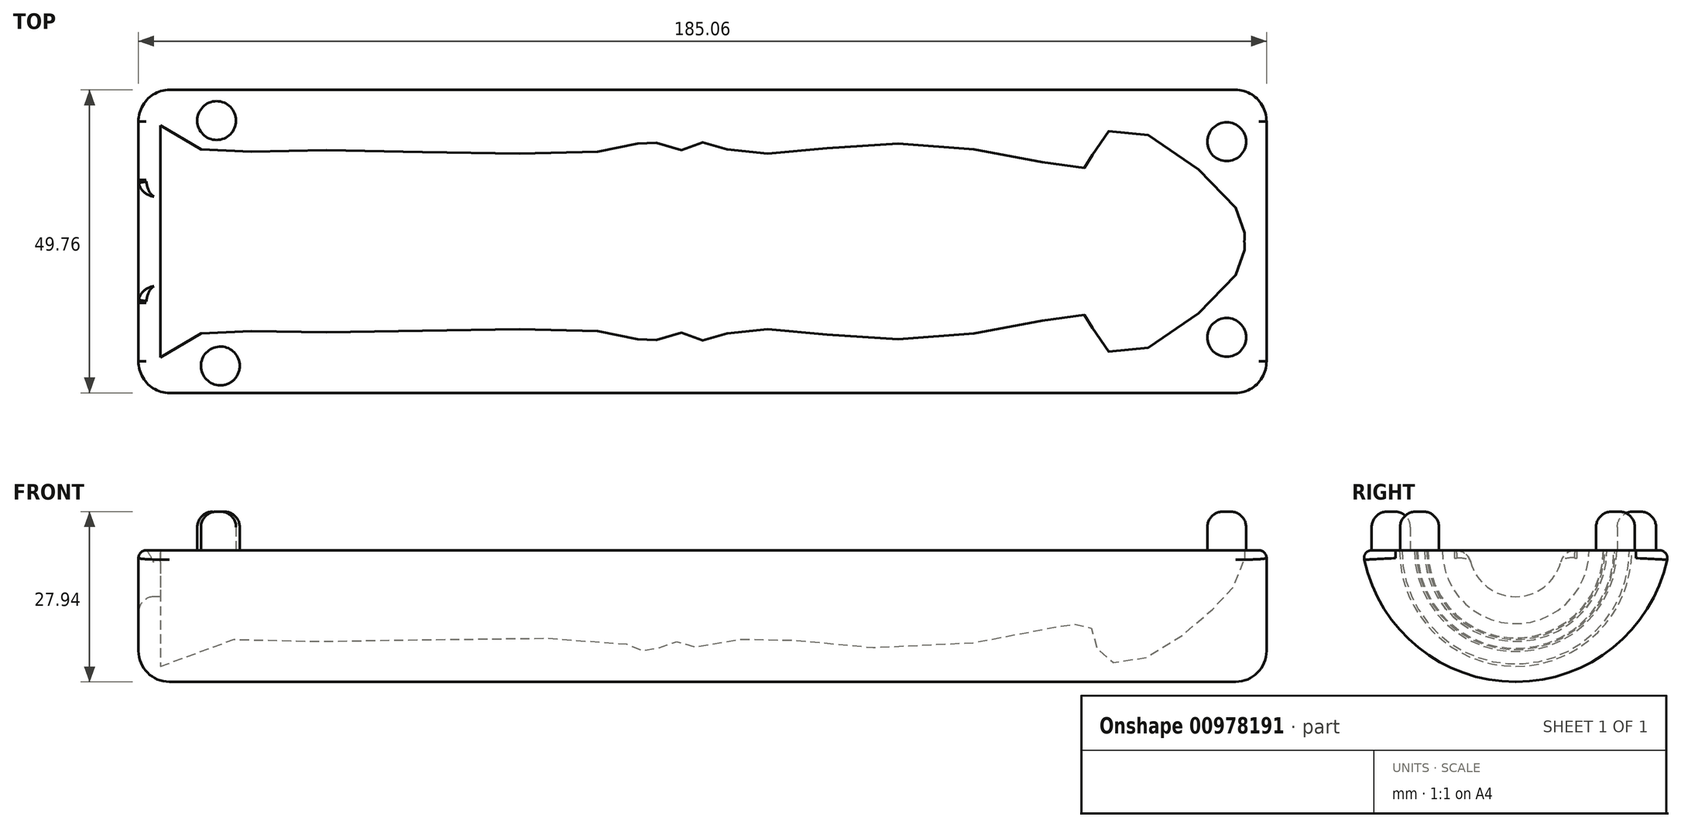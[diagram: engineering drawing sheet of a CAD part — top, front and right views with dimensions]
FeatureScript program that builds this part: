
annotation { "Feature Type Name" : "Feature", "Feature Type Description" : "" }
export const myFeature = defineFeature(function(context is Context, id is Id, definition is map)
    precondition{}
    {
        {
            var Q0;
            Q0=qCreatedBy(makeId("Front.planeOp"),FACE);
            var sketch = newSketch(context, id + "F0", { "sketchPlane" : qUnion([Q0])});
            skLineSegment(sketch, "E0.right", {"start": v(-88.9, 19.05) * mm, "end": v(-88.9, 0) * mm});
            skPoint(sketch, "E0.middle", {"position": v(0, 0) * mm});
            skLineSegment(sketch, "E1", {"start": v(-88.9, 0) * mm, "end": v(88.9, 0) * mm});
            skFitSpline(sketch, "E2", {"points": [v(-88.9, 19.05) * mm, v(-68.88, 14.9) * mm, v(-12.62, 15.36) * mm, v(-8.8, 16.59) * mm, v(-3.86, 14.96) * mm, v(0, 16.28) * mm, v(6.03, 14.62) * mm, v(37.07, 15.98) * mm, v(63.33, 12.23) * mm, v(64, 14.28) * mm, v(68.77, 18.66) * mm, v(87.5, 5.49) * mm, v(88.9, 0) * mm], "startDerivative": vector(153.99, -157.05) * mm, "endDerivative": vector(-4.41, -120.62) * mm});
            skSolve(sketch);
        }
        {
            var Q0;
            Q0=makeQuery(id+"F0.imprint","IMPRINT",FACE,{"disambiguationData":[TD([[makeQuery(id+"F0.imprint","IMPRINT",EDGE,{"derivedFrom":sQuery(id+"F0.wireOp",EDGE,"E0.right")}),1.0]])]});
            var Q1;
            Q1=sQuery(id+"F0.wireOp",EDGE,"E1");
            revolve(context, id + "F1", {"surfaceOperationType" : NewSurfaceOperationType.NEW, "entities" : qUnion([Q0]), "axis" : qUnion([Q1]), "revolveType" : RevolveType.FULL});
        }
        {
            var Q0;
            Q0=qCreatedBy(makeId("Top.planeOp"),FACE);
            var sketch = newSketch(context, id + "F2", { "sketchPlane" : qUnion([Q0])});
            skLineSegment(sketch, "E3.bottom", {"start": v(89.99, 25.13) * mm, "end": v(-89.99, 25.13) * mm});
            skLineSegment(sketch, "E3.top", {"start": v(89.99, -25.13) * mm, "end": v(-89.99, -25.13) * mm});
            skLineSegment(sketch, "E3.left", {"start": v(92.53, 22.59) * mm, "end": v(92.53, -22.59) * mm});
            skLineSegment(sketch, "E3.right", {"start": v(-92.53, 22.59) * mm, "end": v(-92.53, -22.59) * mm});
            skPoint(sketch, "E3.middle", {"position": v(0, 0) * mm});
            skPoint(sketch, "E4.visualSharp", {"position": v(-92.53, 25.13) * mm});
            skArc(sketch, "E4.filletArc", {"start": v(-89.99, 25.13) * mm, "mid": v(-91.78, 24.38) * mm, "end": v(-92.53, 22.59) * mm});
            skPoint(sketch, "E5.visualSharp", {"position": v(-92.53, -25.13) * mm});
            skArc(sketch, "E5.filletArc", {"start": v(-92.53, -22.59) * mm, "mid": v(-91.78, -24.38) * mm, "end": v(-89.99, -25.13) * mm});
            skPoint(sketch, "E6.visualSharp", {"position": v(92.53, 25.13) * mm});
            skArc(sketch, "E6.filletArc", {"start": v(92.53, 22.59) * mm, "mid": v(91.78, 24.38) * mm, "end": v(89.99, 25.13) * mm});
            skPoint(sketch, "E7.visualSharp", {"position": v(92.53, -25.13) * mm});
            skArc(sketch, "E7.filletArc", {"start": v(89.99, -25.13) * mm, "mid": v(91.78, -24.38) * mm, "end": v(92.53, -22.59) * mm});
            skCircle(sketch, "E8", {"center": v(86, 16.37) * mm, "radius": 3.18 * mm});
            skCircle(sketch, "E9", {"center": v(86, -15.77) * mm, "radius": 3.18 * mm});
            skCircle(sketch, "E10", {"center": v(-79.7, 19.84) * mm, "radius": 3.18 * mm});
            skCircle(sketch, "E11", {"center": v(-79.1, -20.45) * mm, "radius": 3.18 * mm});
            skSolve(sketch);
        }
        {
            var Q0;
            Q0=makeQuery(id+"F2.imprint","IMPRINT",FACE,{"disambiguationData":[TD([[makeQuery(id+"F2.imprint","IMPRINT",EDGE,{"derivedFrom":sQuery(id+"F2.wireOp",EDGE,"E3.bottom")}),1.0]])]});
            var Q1;
            Q1=makeQuery(id+"F2.imprint","IMPRINT",FACE,{"disambiguationData":[TD([[makeQuery(id+"F2.imprint","IMPRINT",EDGE,{"derivedFrom":sQuery(id+"F2.wireOp",EDGE,"E8")}),1.0]])]});
            var Q2;
            Q2=makeQuery(id+"F2.imprint","IMPRINT",FACE,{"disambiguationData":[TD([[makeQuery(id+"F2.imprint","IMPRINT",EDGE,{"derivedFrom":sQuery(id+"F2.wireOp",EDGE,"E9")}),1.0]])]});
            var Q3;
            Q3=makeQuery(id+"F2.imprint","IMPRINT",FACE,{"disambiguationData":[TD([[makeQuery(id+"F2.imprint","IMPRINT",EDGE,{"derivedFrom":sQuery(id+"F2.wireOp",EDGE,"E11")}),1.0]])]});
            var Q4;
            Q4=makeQuery(id+"F2.imprint","IMPRINT",FACE,{"disambiguationData":[TD([[makeQuery(id+"F2.imprint","IMPRINT",EDGE,{"derivedFrom":sQuery(id+"F2.wireOp",EDGE,"E10")}),1.0]])]});
            extrude(context, id + "F3", {"entities" : qUnion([Q0, Q1, Q2, Q3, Q4]), "oppositeDirection" : true, "depth" : 21.59 * mm, "offsetDistance" : 25.4 * mm});
        }
        {
            var Q0;
            Q0=makeQuery(id+"F1.opRevolve","SWEPT_BODY",BODY,{"disambiguationData":[OSD([sQuery(id+"F0.wireOp",EDGE,"E0.right"),sQuery(id+"F0.wireOp",EDGE,"E1"),sQuery(id+"F0.wireOp",EDGE,"E2")])]});
            var Q1;
            Q1=makeQuery(id+"F3.opExtrude","SWEPT_BODY",BODY,{"disambiguationData":[OSD([sQuery(id+"F2.wireOp",EDGE,"E3.bottom"),sQuery(id+"F2.wireOp",EDGE,"E3.top"),sQuery(id+"F2.wireOp",EDGE,"E3.left"),sQuery(id+"F2.wireOp",EDGE,"E3.right"),sQuery(id+"F2.wireOp",EDGE,"E4.filletArc"),sQuery(id+"F2.wireOp",EDGE,"E5.filletArc"),sQuery(id+"F2.wireOp",EDGE,"E6.filletArc"),sQuery(id+"F2.wireOp",EDGE,"E7.filletArc")])]});
            booleanBodies(context, id + "F4", {"operationType" : BooleanOperationType.SUBTRACTION, "tools" : qUnion([Q0]), "targets" : qUnion([Q1])});
        }
        {
            var Q0;
            Q0=makeQuery(id+"F3.opExtrude","CAP_EDGE",EDGE,{"disambiguationData":[OSD([sQuery(id+"F2.wireOp",EDGE,"E3.top")])],"isStart":false});
            var Q1;
            Q1=makeQuery(id+"F3.opExtrude","CAP_EDGE",EDGE,{"disambiguationData":[OSD([sQuery(id+"F2.wireOp",EDGE,"E3.bottom")])],"isStart":false});
            fillet(context, id + "F5", {"entities" : qUnion([Q0, Q1]), "radius" : 25.4 * mm, "allowEdgeOverflow" : false});
        }
        {
            var Q0;
            Q0=makeQuery(id+"F5.opFillet","BLEND_EDGE",EDGE,{"blendedFrom":[makeQuery(id+"F3.opExtrude","CAP_EDGE",EDGE,{"disambiguationData":[OSD([sQuery(id+"F2.wireOp",EDGE,"E3.bottom")])],"isStart":false}),makeQuery(id+"F3.opExtrude","SWEPT_FACE",FACE,{"disambiguationData":[OSD([sQuery(id+"F2.wireOp",EDGE,"E3.left")])]})],"blendedInto":[makeQuery(id+"F3.opExtrude","SWEPT_FACE",FACE,{"disambiguationData":[OSD([sQuery(id+"F2.wireOp",EDGE,"E3.left")])]})]});
            var Q1;
            Q1=makeQuery(id+"F5.opFillet","BLEND_EDGE",EDGE,{"blendedFrom":[makeQuery(id+"F3.opExtrude","CAP_EDGE",EDGE,{"disambiguationData":[OSD([sQuery(id+"F2.wireOp",EDGE,"E3.top")])],"isStart":false}),makeQuery(id+"F3.opExtrude","SWEPT_FACE",FACE,{"disambiguationData":[OSD([sQuery(id+"F2.wireOp",EDGE,"E3.right")])]})],"blendedInto":[makeQuery(id+"F3.opExtrude","SWEPT_FACE",FACE,{"disambiguationData":[OSD([sQuery(id+"F2.wireOp",EDGE,"E3.right")])]})]});
            fillet(context, id + "F6", {"entities" : qUnion([Q0, Q1]), "radius" : 5.08 * mm, "tangentPropagation" : true, "allowEdgeOverflow" : false});
        }
        {
            var Q0;
            {var subQ0=sQuery(id+"F2.wireOp",EDGE,"E3.top");Q0=makeQuery(id+"F5.opFillet","BLEND_EDGE",EDGE,{"blendedFrom":[makeQuery(id+"F3.opExtrude","CAP_EDGE",EDGE,{"disambiguationData":[OSD([subQ0])],"isStart":false}),makeQuery(id+"F3.opExtrude","CAP_FACE",FACE,{"disambiguationData":[OSD([sQuery(id+"F2.wireOp",EDGE,"E3.bottom"),subQ0,sQuery(id+"F2.wireOp",EDGE,"E3.left"),sQuery(id+"F2.wireOp",EDGE,"E3.right"),sQuery(id+"F2.wireOp",EDGE,"E4.filletArc"),sQuery(id+"F2.wireOp",EDGE,"E5.filletArc"),sQuery(id+"F2.wireOp",EDGE,"E6.filletArc"),sQuery(id+"F2.wireOp",EDGE,"E7.filletArc")])],"isStart":true})],"blendedInto":[makeQuery(id+"F3.opExtrude","CAP_FACE",FACE,{"disambiguationData":[OSD([sQuery(id+"F2.wireOp",EDGE,"E3.bottom"),subQ0,sQuery(id+"F2.wireOp",EDGE,"E3.left"),sQuery(id+"F2.wireOp",EDGE,"E3.right"),sQuery(id+"F2.wireOp",EDGE,"E4.filletArc"),sQuery(id+"F2.wireOp",EDGE,"E5.filletArc"),sQuery(id+"F2.wireOp",EDGE,"E6.filletArc"),sQuery(id+"F2.wireOp",EDGE,"E7.filletArc")])],"isStart":true})]});}
            fillet(context, id + "F7", {"entities" : qUnion([Q0]), "radius" : 1.27 * mm, "tangentPropagation" : true, "allowEdgeOverflow" : false});
        }
        {
            var Q0;
            Q0=qCreatedBy(makeId("Top.planeOp"),FACE);
            var sketch = newSketch(context, id + "F8", { "sketchPlane" : qUnion([Q0])});
            skLineSegment(sketch, "E12", {"start": v(-96.64, 0) * mm, "end": v(55.98, 0) * mm});
            skLineSegment(sketch, "E13", {"start": v(55.98, 0) * mm, "end": v(55.98, 7.62) * mm});
            skLineSegment(sketch, "E14", {"start": v(55.98, 7.62) * mm, "end": v(-96.64, 7.62) * mm});
            skLineSegment(sketch, "E15", {"start": v(-96.64, 7.62) * mm, "end": v(-96.64, 0) * mm});
            skSolve(sketch);
        }
        {
            var Q0;
            Q0=makeQuery(id+"F8.imprint","IMPRINT",FACE,{"disambiguationData":[TD([[makeQuery(id+"F8.imprint","IMPRINT",EDGE,{"derivedFrom":sQuery(id+"F8.wireOp",EDGE,"E12")}),1.0]])]});
            var Q1;
            Q1=sQuery(id+"F8.wireOp",EDGE,"E12");
            revolve(context, id + "F9", {"surfaceOperationType" : NewSurfaceOperationType.NEW, "entities" : qUnion([Q0]), "axis" : qUnion([Q1]), "revolveType" : RevolveType.FULL});
        }
        {
            var Q0;
            Q0=makeQuery(id+"F9.opRevolve","SWEPT_EDGE",EDGE,{"disambiguationData":[OSD([sQuery(id+"F8.wireOp",EDGE,"E13"),sQuery(id+"F8.wireOp",EDGE,"E14")])]});
            fillet(context, id + "F10", {"entities" : qUnion([Q0]), "radius" : 5.08 * mm, "tangentPropagation" : true, "allowEdgeOverflow" : false});
        }
        {
            var Q0;
            Q0=makeQuery(id+"F9.opRevolve","SWEPT_BODY",BODY,{"disambiguationData":[OSD([sQuery(id+"F8.wireOp",EDGE,"E12"),sQuery(id+"F8.wireOp",EDGE,"E13"),sQuery(id+"F8.wireOp",EDGE,"E14"),sQuery(id+"F8.wireOp",EDGE,"E15")])]});
            var Q1;
            Q1=makeQuery(id+"F3.opExtrude","SWEPT_BODY",BODY,{"disambiguationData":[OSD([sQuery(id+"F2.wireOp",EDGE,"E3.bottom"),sQuery(id+"F2.wireOp",EDGE,"E3.top"),sQuery(id+"F2.wireOp",EDGE,"E3.left"),sQuery(id+"F2.wireOp",EDGE,"E3.right"),sQuery(id+"F2.wireOp",EDGE,"E4.filletArc"),sQuery(id+"F2.wireOp",EDGE,"E5.filletArc"),sQuery(id+"F2.wireOp",EDGE,"E6.filletArc"),sQuery(id+"F2.wireOp",EDGE,"E7.filletArc")])]});
            booleanBodies(context, id + "F11", {"operationType" : BooleanOperationType.SUBTRACTION, "tools" : qUnion([Q0]), "targets" : qUnion([Q1])});
        }
        {
            var Q0;
            Q0=makeQuery(id+"F11.opBoolean","INTERSECT",EDGE,{"derivedFrom":[makeQuery(id+"F3.opExtrude","SWEPT_FACE",FACE,{"disambiguationData":[OSD([sQuery(id+"F2.wireOp",EDGE,"E3.right")])]}),makeQuery(id+"F9.opRevolve","SWEPT_FACE",FACE,{"disambiguationData":[OSD([sQuery(id+"F8.wireOp",EDGE,"E14")])]})]});
            fillet(context, id + "F12", {"entities" : qUnion([Q0]), "radius" : 2.54 * mm, "tangentPropagation" : true, "allowEdgeOverflow" : false});
        }
        {
            var Q0;
            Q0=makeQuery(id+"F2.imprint","IMPRINT",FACE,{"disambiguationData":[TD([[makeQuery(id+"F2.imprint","IMPRINT",EDGE,{"derivedFrom":sQuery(id+"F2.wireOp",EDGE,"E10")}),1.0]])]});
            var Q1;
            Q1=makeQuery(id+"F2.imprint","IMPRINT",FACE,{"disambiguationData":[TD([[makeQuery(id+"F2.imprint","IMPRINT",EDGE,{"derivedFrom":sQuery(id+"F2.wireOp",EDGE,"E11")}),1.0]])]});
            var Q2;
            Q2=makeQuery(id+"F2.imprint","IMPRINT",FACE,{"disambiguationData":[TD([[makeQuery(id+"F2.imprint","IMPRINT",EDGE,{"derivedFrom":sQuery(id+"F2.wireOp",EDGE,"E8")}),1.0]])]});
            var Q3;
            Q3=makeQuery(id+"F2.imprint","IMPRINT",FACE,{"disambiguationData":[TD([[makeQuery(id+"F2.imprint","IMPRINT",EDGE,{"derivedFrom":sQuery(id+"F2.wireOp",EDGE,"E9")}),1.0]])]});
            extrude(context, id + "F13", {"entities" : qUnion([Q0, Q1, Q2, Q3]), "operationType" : NewBodyOperationType.ADD, "depth" : 6.35 * mm, "offsetDistance" : 25.4 * mm});
        }
        {
            var Q0;
            Q0=makeQuery(id+"F13.opExtrude","CAP_EDGE",EDGE,{"disambiguationData":[OSD([sQuery(id+"F2.wireOp",EDGE,"E11")])],"isStart":false});
            var Q1;
            Q1=makeQuery(id+"F13.opExtrude","CAP_EDGE",EDGE,{"disambiguationData":[OSD([sQuery(id+"F2.wireOp",EDGE,"E8")])],"isStart":false});
            var Q2;
            Q2=makeQuery(id+"F13.opExtrude","CAP_EDGE",EDGE,{"disambiguationData":[OSD([sQuery(id+"F2.wireOp",EDGE,"E9")])],"isStart":false});
            var Q3;
            Q3=makeQuery(id+"F13.opExtrude","CAP_EDGE",EDGE,{"disambiguationData":[OSD([sQuery(id+"F2.wireOp",EDGE,"E10")])],"isStart":false});
            fillet(context, id + "F14", {"entities" : qUnion([Q0, Q1, Q2, Q3]), "radius" : 2.54 * mm, "tangentPropagation" : true, "allowEdgeOverflow" : false});
        }
    });
